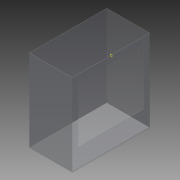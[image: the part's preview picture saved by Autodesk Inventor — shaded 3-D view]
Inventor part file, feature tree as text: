
AUTODESK INVENTOR PART (.ipt)
format: ipt  version: 2013 (Build 170138000, 138)  size: 97,280 bytes
history: native  units: in
note: dims shown in document units (in); Inventor stores cm internally (conversion verified against a paired STEP export)
features: sketch x3, extrude x2, shell x1, hole x1, plane x1
ambient origin geometry x8: Origin, YZ Plane, XZ Plane, XY Plane, X Axis, Y Axis, Z Axis, Center Point
bodies: Solid1 (feature_tree)
feature tree (8):
  extrude  "Extrusion1"  Depth=20.0in
  shell  "Shell1"  Thickness=38.0in
  extrude  "Extrusion2"  Depth=2.75in
  hole  "Hole1"  [1 undecoded]
  plane  "Work Plane1"
  sketch  "Sketch1"  dims[d0=36.0in d1=20.0in d2=38.0in d3=0.0in]
  sketch  "Sketch2"  dims[d4=0.125in d5=2.75in]
  sketch  "Sketch3"  dims[d6=30.5in d7=26.0in d8=9.0in d9=38.0in d10=0.0in d11=0.25in d12=0.75in d13=0.375in d14=0.25in d15=0.5635in d16=1.0in d17=0.8108in]
note: 1 required parameter value undecoded (feature->parameter linkage not recoverable at this tier; creation-order binding heuristic only, values carry confidence <= 0.55)
